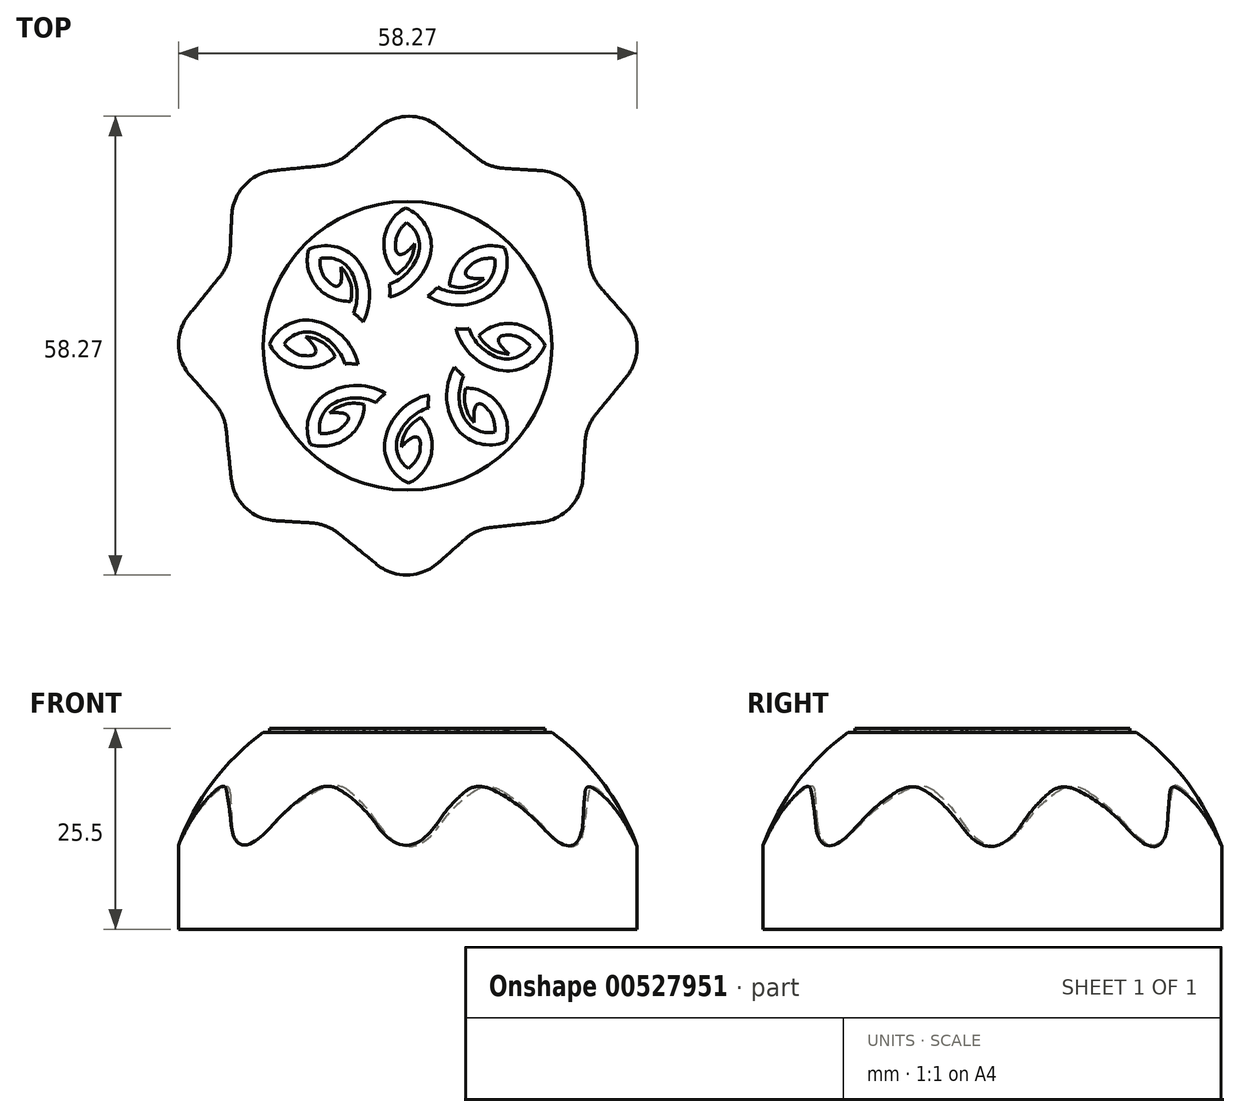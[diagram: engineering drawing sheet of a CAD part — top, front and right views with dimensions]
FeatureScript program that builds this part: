
annotation { "Feature Type Name" : "Feature", "Feature Type Description" : "" }
export const myFeature = defineFeature(function(context is Context, id is Id, definition is map)
    precondition{}
    {
        {
            var Q0;
            Q0=qCreatedBy(makeId("Top.planeOp"),FACE);
            var sketch = newSketch(context, id + "F0", { "sketchPlane" : qUnion([Q0])});
            skLineSegment(sketch, "E0", {"start": v(-3.79, 27.66) * mm, "end": v(-7.53, 24.36) * mm});
            skLineSegment(sketch, "E1", {"start": v(-10.89, 22.89) * mm, "end": v(-16.95, 22.27) * mm});
            skLineSegment(sketch, "E2", {"start": v(-22.53, 12.27) * mm, "end": v(-22.34, 16.57) * mm});
            skLineSegment(sketch, "E3", {"start": v(-23.87, 8.75) * mm, "end": v(-27.76, 3.97) * mm});
            skLineSegment(sketch, "E4", {"start": v(-24.52, -7.29) * mm, "end": v(-27.6, -3.79) * mm});
            skLineSegment(sketch, "E5", {"start": v(-23.05, -10.64) * mm, "end": v(-22.41, -16.83) * mm});
            skLineSegment(sketch, "E6", {"start": v(-16.82, -22.2) * mm, "end": v(-12.16, -22.5) * mm});
            skLineSegment(sketch, "E7", {"start": v(-8.74, -23.83) * mm, "end": v(-3.92, -27.76) * mm});
            skLineSegment(sketch, "E8", {"start": v(3.84, -27.6) * mm, "end": v(7.34, -24.52) * mm});
            skLineSegment(sketch, "E9", {"start": v(10.7, -23.05) * mm, "end": v(16.89, -22.41) * mm});
            skLineSegment(sketch, "E10", {"start": v(22.26, -16.82) * mm, "end": v(22.55, -12.16) * mm});
            skLineSegment(sketch, "E11", {"start": v(23.89, -8.74) * mm, "end": v(27.81, -3.92) * mm});
            skLineSegment(sketch, "E12", {"start": v(27.66, 3.84) * mm, "end": v(24.57, 7.34) * mm});
            skLineSegment(sketch, "E13", {"start": v(23.1, 10.7) * mm, "end": v(22.47, 16.89) * mm});
            skLineSegment(sketch, "E14", {"start": v(16.87, 22.26) * mm, "end": v(12.21, 22.55) * mm});
            skLineSegment(sketch, "E15", {"start": v(8.8, 23.89) * mm, "end": v(3.97, 27.82) * mm});
            skPoint(sketch, "E16.visualSharp", {"position": v(-8.97, 23.08) * mm});
            skArc(sketch, "E16.filletArc", {"start": v(-10.89, 22.89) * mm, "mid": v(-9.1, 23.36) * mm, "end": v(-7.53, 24.36) * mm});
            skPoint(sketch, "E17.visualSharp", {"position": v(0.03, 31.03) * mm});
            skArc(sketch, "E17.filletArc", {"start": v(3.97, 27.82) * mm, "mid": v(0.06, 29.16) * mm, "end": v(-3.79, 27.66) * mm});
            skPoint(sketch, "E18.visualSharp", {"position": v(10.29, 22.67) * mm});
            skArc(sketch, "E18.filletArc", {"start": v(8.8, 23.89) * mm, "mid": v(10.4, 22.95) * mm, "end": v(12.21, 22.55) * mm});
            skPoint(sketch, "E19.visualSharp", {"position": v(21.95, 21.95) * mm});
            skArc(sketch, "E19.filletArc", {"start": v(22.47, 16.89) * mm, "mid": v(20.65, 20.6) * mm, "end": v(16.87, 22.26) * mm});
            skPoint(sketch, "E20.visualSharp", {"position": v(23.3, 8.78) * mm});
            skArc(sketch, "E20.filletArc", {"start": v(23.1, 10.7) * mm, "mid": v(23.57, 8.9) * mm, "end": v(24.57, 7.34) * mm});
            skPoint(sketch, "E21.visualSharp", {"position": v(31.03, 0.03) * mm});
            skArc(sketch, "E21.filletArc", {"start": v(27.81, -3.92) * mm, "mid": v(29.16, 0) * mm, "end": v(27.66, 3.84) * mm});
            skPoint(sketch, "E22.visualSharp", {"position": v(21.95, -21.9) * mm});
            skArc(sketch, "E22.filletArc", {"start": v(16.89, -22.41) * mm, "mid": v(20.6, -20.6) * mm, "end": v(22.26, -16.82) * mm});
            skPoint(sketch, "E23.visualSharp", {"position": v(0.03, -30.97) * mm});
            skArc(sketch, "E23.filletArc", {"start": v(-3.92, -27.76) * mm, "mid": v(-0.01, -29.1) * mm, "end": v(3.84, -27.6) * mm});
            skPoint(sketch, "E24.visualSharp", {"position": v(-21.9, -21.9) * mm});
            skArc(sketch, "E24.filletArc", {"start": v(-22.41, -16.83) * mm, "mid": v(-20.6, -20.55) * mm, "end": v(-16.82, -22.2) * mm});
            skPoint(sketch, "E25.visualSharp", {"position": v(-30.97, 0.03) * mm});
            skArc(sketch, "E25.filletArc", {"start": v(-27.76, 3.97) * mm, "mid": v(-29.1, 0.06) * mm, "end": v(-27.6, -3.79) * mm});
            skPoint(sketch, "E26.visualSharp", {"position": v(-22.1, 21.74) * mm});
            skArc(sketch, "E26.filletArc", {"start": v(-16.95, 22.27) * mm, "mid": v(-20.7, 20.42) * mm, "end": v(-22.34, 16.57) * mm});
            skPoint(sketch, "E27.visualSharp", {"position": v(-23.24, -8.73) * mm});
            skArc(sketch, "E27.filletArc", {"start": v(-23.05, -10.64) * mm, "mid": v(-23.52, -8.85) * mm, "end": v(-24.52, -7.29) * mm});
            skPoint(sketch, "E28.visualSharp", {"position": v(-10.24, -22.62) * mm});
            skArc(sketch, "E28.filletArc", {"start": v(-8.74, -23.83) * mm, "mid": v(-10.35, -22.9) * mm, "end": v(-12.16, -22.5) * mm});
            skPoint(sketch, "E29.visualSharp", {"position": v(8.78, -23.24) * mm});
            skArc(sketch, "E29.filletArc", {"start": v(10.7, -23.05) * mm, "mid": v(8.9, -23.52) * mm, "end": v(7.34, -24.52) * mm});
            skPoint(sketch, "E30.visualSharp", {"position": v(22.67, -10.23) * mm});
            skArc(sketch, "E30.filletArc", {"start": v(23.89, -8.74) * mm, "mid": v(22.95, -10.34) * mm, "end": v(22.55, -12.16) * mm});
            skPoint(sketch, "E31.visualSharp", {"position": v(-22.62, 10.29) * mm});
            skArc(sketch, "E31.filletArc", {"start": v(-23.87, 8.75) * mm, "mid": v(-22.92, 10.4) * mm, "end": v(-22.53, 12.27) * mm});
            skSolve(sketch);
        }
        {
            var Q0;
            Q0=qCreatedBy(makeId("Front.planeOp"),FACE);
            var sketch = newSketch(context, id + "F1", { "sketchPlane" : qUnion([Q0])});
            skArc(sketch, "E32", {"start": v(31, 0) * mm, "mid": v(21.92, 21.92) * mm, "end": v(0, 31) * mm});
            skLineSegment(sketch, "E33", {"start": v(0, 0) * mm, "end": v(31, 0) * mm});
            skLineSegment(sketch, "E34", {"start": v(0, 0) * mm, "end": v(0, 31) * mm});
            skSolve(sketch);
        }
        {
            var Q0;
            Q0=makeQuery(id+"F1.imprint","IMPRINT",FACE,{"disambiguationData":[TD([[makeQuery(id+"F1.imprint","IMPRINT",EDGE,{"derivedFrom":sQuery(id+"F1.wireOp",EDGE,"E32")}),1.0]])]});
            var Q1;
            Q1=sQuery(id+"F1.wireOp",EDGE,"E34");
            revolve(context, id + "F2", {"entities" : qUnion([Q0]), "axis" : qUnion([Q1]), "revolveType" : RevolveType.FULL});
        }
        {
            var Q0;
            Q0=qSketchRegion(id+"F0",true);
            extrude(context, id + "F3", {"entities" : qUnion([Q0]), "operationType" : NewBodyOperationType.INTERSECT, "depth" : 25 * mm, "offsetDistance" : 25 * mm});
        }
        {
            var Q0;
            Q0=qCreatedBy(makeId("Top.planeOp"),FACE);
            var sketch = newSketch(context, id + "F4", { "sketchPlane" : qUnion([Q0])});
            skArc(sketch, "E35", {"start": v(-17.53, 0.22) * mm, "mid": v(-13.76, -2.67) * mm, "end": v(-9.2, -1.36) * mm});
            skArc(sketch, "E36", {"start": v(-12.06, 3.22) * mm, "mid": v(-15.3, 2.63) * mm, "end": v(-17.53, 0.22) * mm});
            skArc(sketch, "E37", {"start": v(-6.3, -2.36) * mm, "mid": v(-8.34, 1.3) * mm, "end": v(-12.06, 3.22) * mm});
            skArc(sketch, "E38", {"start": v(-6.3, -2.36) * mm, "mid": v(-7.13, -2.28) * mm, "end": v(-7.97, -2.29) * mm});
            skArc(sketch, "E39", {"start": v(-7.97, -2.29) * mm, "mid": v(-9.28, -0.01) * mm, "end": v(-11.43, 1.5) * mm});
            skArc(sketch, "E40", {"start": v(-11.43, 1.5) * mm, "mid": v(-13.77, 1.62) * mm, "end": v(-15.68, 0.25) * mm});
            skArc(sketch, "E41", {"start": v(-15.68, 0.25) * mm, "mid": v(-14.82, -0.58) * mm, "end": v(-13.76, -1.15) * mm});
            skArc(sketch, "E42", {"start": v(-9.2, -1.36) * mm, "mid": v(-10.73, 0.39) * mm, "end": v(-12.94, 1.15) * mm});
            skFitSpline(sketch, "E43", {"points": [v(-13.76, -1.15) * mm, v(-12.94, -1.26) * mm, v(-12.08, -1.22) * mm, v(-11.72, -0.95) * mm, v(-11.67, -0.46) * mm, v(-11.96, 0.08) * mm, v(-12.35, 0.57) * mm, v(-12.94, 1.15) * mm], "startDerivative": vector(7.77, -1.7) * mm, "endDerivative": vector(-3.9, 3.72) * mm});
            skArc(sketch, "E44", {"start": v(-12.34, -12.51) * mm, "mid": v(-7.66, -11.71) * mm, "end": v(-5.51, -7.47) * mm});
            skArc(sketch, "E45", {"start": v(-10.82, -6.46) * mm, "mid": v(-12.59, -9.23) * mm, "end": v(-12.34, -12.51) * mm});
            skArc(sketch, "E46", {"start": v(-2.81, -6.03) * mm, "mid": v(-6.88, -5.04) * mm, "end": v(-10.82, -6.46) * mm});
            skArc(sketch, "E47", {"start": v(-2.81, -6.03) * mm, "mid": v(-3.44, -6.58) * mm, "end": v(-4, -7.2) * mm});
            skArc(sketch, "E48", {"start": v(-4, -7.2) * mm, "mid": v(-6.56, -6.62) * mm, "end": v(-9.13, -7.17) * mm});
            skArc(sketch, "E49", {"start": v(-9.13, -7.17) * mm, "mid": v(-10.81, -8.8) * mm, "end": v(-11.1, -11.13) * mm});
            skArc(sketch, "E50", {"start": v(-11.1, -11.13) * mm, "mid": v(-9.9, -11.07) * mm, "end": v(-8.77, -10.68) * mm});
            skArc(sketch, "E51", {"start": v(-5.51, -7.47) * mm, "mid": v(-7.84, -7.41) * mm, "end": v(-9.9, -8.51) * mm});
            skFitSpline(sketch, "E52", {"points": [v(-8.77, -10.68) * mm, v(-8.14, -10.15) * mm, v(-7.58, -9.5) * mm, v(-7.53, -9.04) * mm, v(-7.86, -8.68) * mm, v(-8.45, -8.52) * mm, v(-9.07, -8.48) * mm, v(-9.9, -8.51) * mm], "startDerivative": vector(6.53, 4.54) * mm, "endDerivative": vector(-5.38, -0.34) * mm});
            skArc(sketch, "E53", {"start": v(-12.58, 12.23) * mm, "mid": v(-11.55, 7.59) * mm, "end": v(-7.21, 5.65) * mm});
            skArc(sketch, "E54", {"start": v(-6.47, 11) * mm, "mid": v(-9.32, 12.63) * mm, "end": v(-12.58, 12.23) * mm});
            skArc(sketch, "E55", {"start": v(-5.64, 3.03) * mm, "mid": v(-4.85, 7.14) * mm, "end": v(-6.47, 11) * mm});
            skArc(sketch, "E56", {"start": v(-5.64, 3.03) * mm, "mid": v(-6.22, 3.62) * mm, "end": v(-6.87, 4.15) * mm});
            skArc(sketch, "E57", {"start": v(-6.87, 4.15) * mm, "mid": v(-6.41, 6.74) * mm, "end": v(-7.1, 9.28) * mm});
            skArc(sketch, "E58", {"start": v(-7.1, 9.28) * mm, "mid": v(-8.8, 10.88) * mm, "end": v(-11.14, 11.06) * mm});
            skArc(sketch, "E59", {"start": v(-11.14, 11.06) * mm, "mid": v(-11.02, 9.86) * mm, "end": v(-10.58, 8.75) * mm});
            skArc(sketch, "E60", {"start": v(-7.21, 5.65) * mm, "mid": v(-7.27, 7.98) * mm, "end": v(-8.47, 9.98) * mm});
            skFitSpline(sketch, "E61", {"points": [v(-10.58, 8.75) * mm, v(-10.02, 8.14) * mm, v(-9.34, 7.62) * mm, v(-8.88, 7.6) * mm, v(-8.53, 7.93) * mm, v(-8.4, 8.54) * mm, v(-8.4, 9.16) * mm, v(-8.47, 9.98) * mm], "startDerivative": vector(4.85, -6.3) * mm, "endDerivative": vector(-0.6, 5.36) * mm});
            skArc(sketch, "E62", {"start": v(17.47, 0.05) * mm, "mid": v(13.58, 2.8) * mm, "end": v(9.07, 1.3) * mm});
            skArc(sketch, "E63", {"start": v(12.12, -3.16) * mm, "mid": v(15.33, -2.44) * mm, "end": v(17.47, 0.05) * mm});
            skArc(sketch, "E64", {"start": v(6.14, 2.18) * mm, "mid": v(8.33, -1.4) * mm, "end": v(12.12, -3.16) * mm});
            skArc(sketch, "E65", {"start": v(6.14, 2.18) * mm, "mid": v(6.97, 2.14) * mm, "end": v(7.8, 2.18) * mm});
            skArc(sketch, "E66", {"start": v(7.8, 2.18) * mm, "mid": v(9.2, -0.04) * mm, "end": v(11.42, -1.46) * mm});
            skArc(sketch, "E67", {"start": v(11.42, -1.46) * mm, "mid": v(13.76, -1.5) * mm, "end": v(15.61, -0.05) * mm});
            skArc(sketch, "E68", {"start": v(15.61, -0.05) * mm, "mid": v(14.72, 0.75) * mm, "end": v(13.64, 1.27) * mm});
            skArc(sketch, "E69", {"start": v(9.07, 1.3) * mm, "mid": v(10.68, -0.39) * mm, "end": v(12.91, -1.05) * mm});
            skFitSpline(sketch, "E70", {"points": [v(13.64, 1.27) * mm, v(12.82, 1.35) * mm, v(11.96, 1.28) * mm, v(11.6, 0.99) * mm, v(11.58, 0.5) * mm, v(11.9, -0.03) * mm, v(12.3, -0.5) * mm, v(12.91, -1.05) * mm], "startDerivative": vector(-7.83, 1.4) * mm, "endDerivative": vector(4.05, -3.56) * mm});
            skArc(sketch, "E71", {"start": v(12.33, 12.43) * mm, "mid": v(7.62, 11.8) * mm, "end": v(5.32, 7.65) * mm});
            skArc(sketch, "E72", {"start": v(10.59, 6.44) * mm, "mid": v(12.46, 9.15) * mm, "end": v(12.33, 12.43) * mm});
            skArc(sketch, "E73", {"start": v(2.57, 6.31) * mm, "mid": v(6.6, 5.17) * mm, "end": v(10.59, 6.44) * mm});
            skArc(sketch, "E74", {"start": v(2.57, 6.31) * mm, "mid": v(3.2, 6.85) * mm, "end": v(3.8, 7.44) * mm});
            skArc(sketch, "E75", {"start": v(3.8, 7.44) * mm, "mid": v(6.33, 6.76) * mm, "end": v(8.92, 7.22) * mm});
            skArc(sketch, "E76", {"start": v(8.92, 7.22) * mm, "mid": v(10.66, 8.78) * mm, "end": v(11.04, 11.1) * mm});
            skArc(sketch, "E77", {"start": v(11.04, 11.1) * mm, "mid": v(9.84, 11.08) * mm, "end": v(8.7, 10.74) * mm});
            skArc(sketch, "E78", {"start": v(5.32, 7.65) * mm, "mid": v(7.64, 7.5) * mm, "end": v(9.74, 8.53) * mm});
            skFitSpline(sketch, "E79", {"points": [v(8.7, 10.74) * mm, v(8.04, 10.23) * mm, v(7.46, 9.6) * mm, v(7.4, 9.15) * mm, v(7.7, 8.77) * mm, v(8.3, 8.6) * mm, v(8.91, 8.53) * mm, v(9.74, 8.53) * mm], "startDerivative": vector(-6.7, -4.28) * mm, "endDerivative": vector(5.39, 0.13) * mm});
            skArc(sketch, "E80", {"start": v(-0.27, 17.51) * mm, "mid": v(-2.97, 13.6) * mm, "end": v(-1.43, 9.1) * mm});
            skArc(sketch, "E81", {"start": v(3, 12.2) * mm, "mid": v(2.25, 15.4) * mm, "end": v(-0.27, 17.51) * mm});
            skArc(sketch, "E82", {"start": v(-2.28, 6.17) * mm, "mid": v(1.27, 8.4) * mm, "end": v(3, 12.2) * mm});
            skArc(sketch, "E83", {"start": v(-2.28, 6.17) * mm, "mid": v(-2.25, 7) * mm, "end": v(-2.3, 7.83) * mm});
            skArc(sketch, "E84", {"start": v(-2.3, 7.83) * mm, "mid": v(-0.09, 9.26) * mm, "end": v(1.3, 11.48) * mm});
            skArc(sketch, "E85", {"start": v(1.3, 11.48) * mm, "mid": v(1.32, 13.83) * mm, "end": v(-0.15, 15.66) * mm});
            skArc(sketch, "E86", {"start": v(-0.15, 15.66) * mm, "mid": v(-0.94, 14.76) * mm, "end": v(-1.45, 13.68) * mm});
            skArc(sketch, "E87", {"start": v(-1.43, 9.1) * mm, "mid": v(0.24, 10.73) * mm, "end": v(0.88, 12.97) * mm});
            skFitSpline(sketch, "E88", {"points": [v(-1.45, 13.68) * mm, v(-1.52, 12.86) * mm, v(-1.44, 12) * mm, v(-1.15, 11.65) * mm, v(-0.66, 11.63) * mm, v(-0.13, 11.94) * mm, v(0.33, 12.36) * mm, v(0.88, 12.97) * mm], "startDerivative": vector(-1.31, -7.84) * mm, "endDerivative": vector(3.52, 4.09) * mm});
            skArc(sketch, "E89", {"start": v(0.13, -17.45) * mm, "mid": v(3.02, -13.68) * mm, "end": v(1.71, -9.11) * mm});
            skArc(sketch, "E90", {"start": v(-2.87, -11.98) * mm, "mid": v(-2.28, -15.21) * mm, "end": v(0.13, -17.45) * mm});
            skArc(sketch, "E91", {"start": v(2.71, -6.22) * mm, "mid": v(-0.95, -8.26) * mm, "end": v(-2.87, -11.98) * mm});
            skArc(sketch, "E92", {"start": v(2.71, -6.22) * mm, "mid": v(2.63, -7.05) * mm, "end": v(2.64, -7.88) * mm});
            skArc(sketch, "E93", {"start": v(2.64, -7.88) * mm, "mid": v(0.36, -9.2) * mm, "end": v(-1.14, -11.35) * mm});
            skArc(sketch, "E94", {"start": v(-1.14, -11.35) * mm, "mid": v(-1.27, -13.69) * mm, "end": v(0.1, -15.6) * mm});
            skArc(sketch, "E95", {"start": v(0.1, -15.6) * mm, "mid": v(0.94, -14.74) * mm, "end": v(1.5, -13.68) * mm});
            skArc(sketch, "E96", {"start": v(1.71, -9.11) * mm, "mid": v(-0.04, -10.65) * mm, "end": v(-0.8, -12.86) * mm});
            skFitSpline(sketch, "E97", {"points": [v(1.5, -13.68) * mm, v(1.6, -12.86) * mm, v(1.57, -12) * mm, v(1.3, -11.64) * mm, v(0.81, -11.59) * mm, v(0.27, -11.88) * mm, v(-0.21, -12.27) * mm, v(-0.8, -12.86) * mm], "startDerivative": vector(1.7, 7.77) * mm, "endDerivative": vector(-3.72, -3.9) * mm});
            skArc(sketch, "E98", {"start": v(12.46, -12.18) * mm, "mid": v(11.65, -7.5) * mm, "end": v(7.4, -5.36) * mm});
            skArc(sketch, "E99", {"start": v(6.4, -10.67) * mm, "mid": v(9.18, -12.43) * mm, "end": v(12.46, -12.18) * mm});
            skArc(sketch, "E100", {"start": v(5.96, -2.66) * mm, "mid": v(4.98, -6.74) * mm, "end": v(6.4, -10.67) * mm});
            skArc(sketch, "E101", {"start": v(5.96, -2.66) * mm, "mid": v(6.51, -3.29) * mm, "end": v(7.13, -3.84) * mm});
            skArc(sketch, "E102", {"start": v(7.13, -3.84) * mm, "mid": v(6.55, -6.4) * mm, "end": v(7.11, -8.97) * mm});
            skArc(sketch, "E103", {"start": v(7.11, -8.97) * mm, "mid": v(8.75, -10.65) * mm, "end": v(11.07, -10.94) * mm});
            skArc(sketch, "E104", {"start": v(11.07, -10.94) * mm, "mid": v(11.01, -9.74) * mm, "end": v(10.62, -8.61) * mm});
            skArc(sketch, "E105", {"start": v(7.4, -5.36) * mm, "mid": v(7.35, -7.69) * mm, "end": v(8.46, -9.74) * mm});
            skFitSpline(sketch, "E106", {"points": [v(10.62, -8.61) * mm, v(10.09, -7.98) * mm, v(9.43, -7.42) * mm, v(8.98, -7.37) * mm, v(8.62, -7.7) * mm, v(8.46, -8.3) * mm, v(8.42, -8.92) * mm, v(8.46, -9.74) * mm], "startDerivative": vector(-4.55, 6.52) * mm, "endDerivative": vector(0.35, -5.38) * mm});
            skSolve(sketch);
        }
        {
            var Q0;
            Q0=qSketchRegion(id+"F4",true);
            extrude(context, id + "F5", {"entities" : qUnion([Q0]), "operationType" : NewBodyOperationType.ADD, "depth" : 25.5 * mm, "offsetDistance" : 25 * mm});
        }
    });
